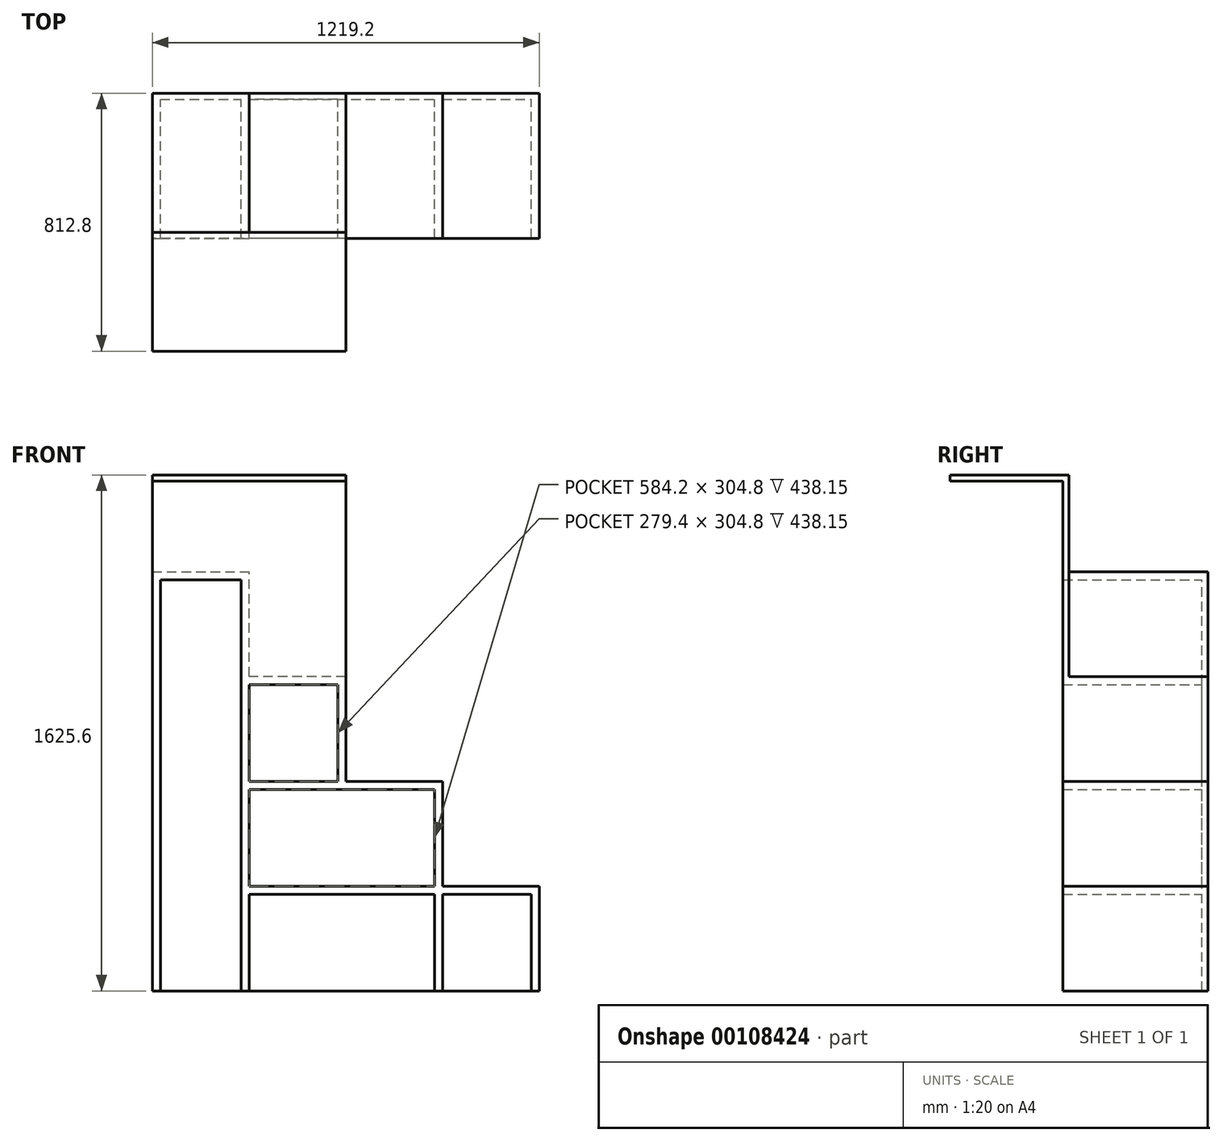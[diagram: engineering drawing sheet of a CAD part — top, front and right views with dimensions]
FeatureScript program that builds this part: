
annotation { "Feature Type Name" : "Feature", "Feature Type Description" : "" }
export const myFeature = defineFeature(function(context is Context, id is Id, definition is map)
    precondition{}
    {
        {
            var Q0;
            Q0=qCreatedBy(makeId("Front.planeOp"),FACE);
            var sketch = newSketch(context, id + "F0", { "sketchPlane" : qUnion([Q0])});
            skLineSegment(sketch, "E0.bottom", {"start": v(0, 0) * mm, "end": v(1219.2, 0) * mm});
            skLineSegment(sketch, "E0.top", {"start": v(0, 1320.8) * mm, "end": v(304.8, 1320.8) * mm});
            skLineSegment(sketch, "E0.left", {"start": v(0, 0) * mm, "end": v(0, 1320.8) * mm});
            skLineSegment(sketch, "E0.right", {"start": v(1219.2, 0) * mm, "end": v(1219.2, 330.2) * mm});
            skLineSegment(sketch, "E1", {"start": v(1219.2, 330.2) * mm, "end": v(914.4, 330.2) * mm});
            skLineSegment(sketch, "E2", {"start": v(914.4, 330.2) * mm, "end": v(914.4, 660.4) * mm});
            skLineSegment(sketch, "E3", {"start": v(914.4, 660.4) * mm, "end": v(609.6, 660.4) * mm});
            skLineSegment(sketch, "E4", {"start": v(609.6, 660.4) * mm, "end": v(609.6, 990.6) * mm});
            skLineSegment(sketch, "E5", {"start": v(609.6, 990.6) * mm, "end": v(304.8, 990.6) * mm});
            skLineSegment(sketch, "E6", {"start": v(304.8, 990.6) * mm, "end": v(304.8, 1320.8) * mm});
            skSolve(sketch);
        }
        {
            var Q0;
            Q0=qSketchRegion(id+"F0",true);
            extrude(context, id + "F1", {"entities" : qUnion([Q0]), "depth" : 19.05 * mm});
        }
        {
            var Q0;
            Q0=makeQuery(id+"F1.opExtrude","CAP_FACE",FACE,{"disambiguationData":[OSD([sQuery(id+"F0.wireOp",EDGE,"E0.bottom"),sQuery(id+"F0.wireOp",EDGE,"E0.top"),sQuery(id+"F0.wireOp",EDGE,"E0.left"),sQuery(id+"F0.wireOp",EDGE,"E0.right"),sQuery(id+"F0.wireOp",EDGE,"E1"),sQuery(id+"F0.wireOp",EDGE,"E2"),sQuery(id+"F0.wireOp",EDGE,"E3"),sQuery(id+"F0.wireOp",EDGE,"E4"),sQuery(id+"F0.wireOp",EDGE,"E5"),sQuery(id+"F0.wireOp",EDGE,"E6")])],"isStart":false});
            var sketch = newSketch(context, id + "F2", { "sketchPlane" : qUnion([Q0])});
            skLineSegment(sketch, "E7.0", {"start": v(1219.2, 0) * mm, "end": v(1219.2, 330.2) * mm});
            skLineSegment(sketch, "E8.0", {"start": v(1219.2, 330.2) * mm, "end": v(914.4, 330.2) * mm});
            skLineSegment(sketch, "E9.0", {"start": v(914.4, 330.2) * mm, "end": v(914.4, 660.4) * mm});
            skLineSegment(sketch, "E10.0", {"start": v(914.4, 660.4) * mm, "end": v(609.6, 660.4) * mm});
            skLineSegment(sketch, "E11.0", {"start": v(609.6, 660.4) * mm, "end": v(609.6, 990.6) * mm});
            skLineSegment(sketch, "E12.0", {"start": v(609.6, 990.6) * mm, "end": v(304.8, 990.6) * mm});
            skLineSegment(sketch, "E13.0", {"start": v(304.8, 990.6) * mm, "end": v(304.8, 1320.8) * mm});
            skLineSegment(sketch, "E14.0", {"start": v(0, 1320.8) * mm, "end": v(304.8, 1320.8) * mm});
            skLineSegment(sketch, "E15.0", {"start": v(279.4, 0) * mm, "end": v(279.4, 1295.4) * mm});
            skLineSegment(sketch, "E16.0", {"start": v(584.2, 965.2) * mm, "end": v(304.8, 965.2) * mm});
            skLineSegment(sketch, "E17.0", {"start": v(889, 635) * mm, "end": v(304.8, 635) * mm});
            skLineSegment(sketch, "E18.0", {"start": v(1193.8, 304.8) * mm, "end": v(914.4, 304.8) * mm});
            skLineSegment(sketch, "E19.0", {"start": v(1193.8, 0) * mm, "end": v(1193.8, 304.8) * mm});
            skLineSegment(sketch, "E20", {"start": v(0, 1320.8) * mm, "end": v(0, 0) * mm});
            skLineSegment(sketch, "E21", {"start": v(1193.8, 0) * mm, "end": v(1219.2, 0) * mm});
            skLineSegment(sketch, "E22", {"start": v(304.8, 965.2) * mm, "end": v(304.8, 660.4) * mm});
            skLineSegment(sketch, "E23", {"start": v(304.8, 0) * mm, "end": v(279.4, 0) * mm});
            skLineSegment(sketch, "E24.0", {"start": v(584.2, 660.4) * mm, "end": v(584.2, 965.2) * mm});
            skLineSegment(sketch, "E25.0", {"start": v(889, 0) * mm, "end": v(889, 304.8) * mm});
            skLineSegment(sketch, "E26", {"start": v(914.4, 304.8) * mm, "end": v(914.4, 0) * mm});
            skLineSegment(sketch, "E27", {"start": v(914.4, 0) * mm, "end": v(889, 0) * mm});
            skLineSegment(sketch, "E28.trimOffspring", {"start": v(889, 304.8) * mm, "end": v(304.8, 304.8) * mm});
            skLineSegment(sketch, "E29", {"start": v(889, 330.2) * mm, "end": v(304.8, 330.2) * mm});
            skLineSegment(sketch, "E30.trimOffspring", {"start": v(889, 330.2) * mm, "end": v(889, 635) * mm});
            skLineSegment(sketch, "E31.0", {"start": v(25.4, 1295.4) * mm, "end": v(25.4, 0) * mm});
            skLineSegment(sketch, "E32.0", {"start": v(25.4, 1295.4) * mm, "end": v(279.4, 1295.4) * mm});
            skLineSegment(sketch, "E33", {"start": v(584.2, 660.4) * mm, "end": v(304.8, 660.4) * mm});
            skLineSegment(sketch, "E34.trimOffspring", {"start": v(304.8, 635) * mm, "end": v(304.8, 330.2) * mm});
            skLineSegment(sketch, "E35.trimOffspring", {"start": v(304.8, 304.8) * mm, "end": v(304.8, 0) * mm});
            skLineSegment(sketch, "E36", {"start": v(25.4, 0) * mm, "end": v(0, 0) * mm});
            skSolve(sketch);
        }
        {
            var Q0;
            Q0=qSketchRegion(id+"F2",true);
            extrude(context, id + "F3", {"entities" : qUnion([Q0]), "operationType" : NewBodyOperationType.ADD, "depth" : 438.15 * mm});
        }
        {
            var Q0;
            Q0=makeQuery(id+"F3.opExtrude","CAP_FACE",FACE,{"disambiguationData":[OSD([sQuery(id+"F2.wireOp",EDGE,"E7.0"),sQuery(id+"F2.wireOp",EDGE,"E8.0"),sQuery(id+"F2.wireOp",EDGE,"E9.0"),sQuery(id+"F2.wireOp",EDGE,"E10.0"),sQuery(id+"F2.wireOp",EDGE,"E11.0"),sQuery(id+"F2.wireOp",EDGE,"E12.0"),sQuery(id+"F2.wireOp",EDGE,"E13.0"),sQuery(id+"F2.wireOp",EDGE,"E14.0"),sQuery(id+"F2.wireOp",EDGE,"578f65b1-47bd-45c8-be6b-978ce24831c3.0"),sQuery(id+"F2.wireOp",EDGE,"E15.0"),sQuery(id+"F2.wireOp",EDGE,"E16.0"),sQuery(id+"F2.wireOp",EDGE,"2b9e4932-af1e-45f5-b4a5-91bd25a9e3da.0"),sQuery(id+"F2.wireOp",EDGE,"E17.0"),sQuery(id+"F2.wireOp",EDGE,"07aff2f9-5ec2-401e-a384-1631a075b325.0"),sQuery(id+"F2.wireOp",EDGE,"E18.0"),sQuery(id+"F2.wireOp",EDGE,"E19.0"),sQuery(id+"F2.wireOp",EDGE,"E20"),sQuery(id+"F2.wireOp",EDGE,"E21")])],"isStart":false});
            var sketch = newSketch(context, id + "F4", { "sketchPlane" : qUnion([Q0])});
            skLineSegment(sketch, "E37", {"start": v(609.6, 1625.6) * mm, "end": v(609.6, 990.6) * mm});
            skLineSegment(sketch, "E38", {"start": v(0, 1320.8) * mm, "end": v(0, 1625.6) * mm});
            skLineSegment(sketch, "E39", {"start": v(0, 1625.6) * mm, "end": v(609.6, 1625.6) * mm});
            skPoint(sketch, "E40.0.start.orphan", {"position": v(609.6, 660.4) * mm});
            skLineSegment(sketch, "E41.0", {"start": v(0, 1320.8) * mm, "end": v(304.8, 1320.8) * mm});
            skLineSegment(sketch, "E42.0", {"start": v(304.8, 990.6) * mm, "end": v(304.8, 1320.8) * mm});
            skLineSegment(sketch, "E43.0", {"start": v(609.6, 990.6) * mm, "end": v(304.8, 990.6) * mm});
            skSolve(sketch);
        }
        {
            var Q0;
            Q0=qSketchRegion(id+"F4",true);
            extrude(context, id + "F5", {"entities" : qUnion([Q0]), "operationType" : NewBodyOperationType.ADD, "oppositeDirection" : true, "depth" : 19.05 * mm});
        }
        {
            var Q0;
            Q0=makeQuery(id+"F5.boolean.opBoolean","MERGE",FACE,{"derivedFrom":[makeQuery(id+"F3.boolean.opBoolean","MERGE",FACE,{"derivedFrom":[makeQuery(id+"F1.opExtrude","SWEPT_FACE",FACE,{"disambiguationData":[OSD([sQuery(id+"F0.wireOp",EDGE,"E0.left")])]}),makeQuery(id+"F3.opExtrude","SWEPT_FACE",FACE,{"disambiguationData":[OSD([sQuery(id+"F2.wireOp",EDGE,"E20")])]})]}),makeQuery(id+"F5.opExtrude","SWEPT_FACE",FACE,{"disambiguationData":[OSD([sQuery(id+"F4.wireOp",EDGE,"71024860-b361-4742-942d-b6376bb1158f.0"),sQuery(id+"F4.wireOp",EDGE,"E38")])]})]});
            var sketch = newSketch(context, id + "F6", { "sketchPlane" : qUnion([Q0])});
            skLineSegment(sketch, "E44", {"start": v(812.8, 1625.6) * mm, "end": v(438.15, 1625.6) * mm});
            skLineSegment(sketch, "E45.0", {"start": v(812.8, 1606.55) * mm, "end": v(438.15, 1606.55) * mm});
            skLineSegment(sketch, "E46", {"start": v(438.15, 1625.6) * mm, "end": v(438.15, 1606.55) * mm});
            skLineSegment(sketch, "E47", {"start": v(812.8, 1606.55) * mm, "end": v(812.8, 1625.6) * mm});
            skSolve(sketch);
        }
        {
            var Q0;
            Q0=qSketchRegion(id+"F6",true);
            var Q1;
            Q1=makeQuery(id+"F5.boolean.opBoolean","MERGE",FACE,{"derivedFrom":[makeQuery(id+"F3.boolean.opBoolean","MERGE",FACE,{"derivedFrom":[makeQuery(id+"F1.opExtrude","SWEPT_FACE",FACE,{"disambiguationData":[OSD([sQuery(id+"F0.wireOp",EDGE,"E4")])]}),makeQuery(id+"F3.opExtrude","SWEPT_FACE",FACE,{"disambiguationData":[OSD([sQuery(id+"F2.wireOp",EDGE,"E11.0")])]})]}),makeQuery(id+"F5.opExtrude","SWEPT_FACE",FACE,{"disambiguationData":[OSD([sQuery(id+"F4.wireOp",EDGE,"E40.0"),sQuery(id+"F4.wireOp",EDGE,"E37")])]})]});
            extrude(context, id + "F7", {"entities" : qUnion([Q0]), "operationType" : NewBodyOperationType.ADD, "endBound" : BoundingType.UP_TO_SURFACE, "oppositeDirection" : true, "endBoundEntityFace" : qUnion([Q1]), "depth" : 25.4 * mm});
        }
    });
